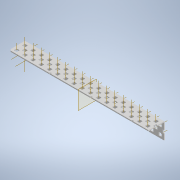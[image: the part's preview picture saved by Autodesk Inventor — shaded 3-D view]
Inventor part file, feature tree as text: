
AUTODESK INVENTOR PART (.ipt)
format: ipt  version: 2020 (Build 240168000, 168)  size: 2,144,256 bytes
history: native  units: in
note: dims shown in document units (in); Inventor stores cm internally (conversion verified against a paired STEP export)
features: other x107, pattern_linear x4, plane x2, sheet_metal_op x1, extrude x1, split x1, imported_body x1, sketch x1
ambient origin geometry x8: Origin, YZ Plane, XZ Plane, XY Plane, X Axis, Y Axis, Z Axis, Center Point
bodies: Body1 (feature_tree)
feature tree (118):
  sheet_metal_op  "Fold1"
  other  "L-Channel"
  extrude  "length cut"  Depth=0.5in
  other  "top out axis"
  other  "top inner axis"
  other  "back out axis"
  other  "back inner axis"
  pattern_linear  "top outer axes"  Count1=2 Spacing1=0.5in
  pattern_linear  "top inner axes"  Spacing1=0.5in  [1 undecoded]
  pattern_linear  "back outer axes"  Count1=2 Spacing1=0.5in
  pattern_linear  "back inner axes"  Spacing1=0.5in  [1 undecoded]
  other  "right plane"
  plane  "Work Plane3"
  split  "Split1"
  plane  "Work Plane5"
  imported_body  "Base1"
  sketch  "Sketch1"  dims[d1=0.0in d4=0.5in d5=0.7874in d7=0.5in d10=0.5in d13=0.5in d14=0.7874in d16=0.5in d19=0.5in d20=-9.0in d21=0.0in d22=0.0in d23=0.0in d24=0.0in d25=0.0in d26=0.0in]
  other  "Work Point1"
  other  "Work Point2"
  other  "Work Point3"
  other  "Work Point4"
  other  "Work Axis5"
  other  "Work Axis6"
  other  "Work Axis7"
  other  "Work Axis8"
  other  "Work Axis11"
  other  "Work Axis12"
  other  "Work Axis13"
  other  "Work Axis14"
  other  "Work Axis15"
  other  "Work Axis18"
  other  "Work Axis19"
  other  "Work Axis20"
  other  "Work Axis23"
  other  "Work Axis24"
  other  "Work Axis25"
  other  "Work Axis26"
  other  "Work Axis29"
  other  "Work Axis30"
  other  "Work Axis31"
  other  "Work Axis32"
  other  "Work Axis33"
  other  "Work Axis36"
  other  "Work Axis37"
  other  "Work Axis38"
  other  "Work Axis41"
  other  "Work Axis42"
  other  "Work Axis43"
  other  "Work Axis44"
  other  "Work Axis45"
  other  "Work Axis46"
  other  "Work Axis47"
  other  "Work Axis48"
  other  "Work Axis49"
  other  "Work Axis50"
  other  "Work Axis51"
  other  "Work Axis52"
  other  "Work Axis61"
  other  "Work Axis62"
  other  "Work Axis63"
  other  "Work Axis64"
  other  "Work Axis65"
  other  "Work Axis66"
  other  "Work Axis67"
  other  "Work Axis68"
  other  "Work Axis69"
  other  "Work Axis70"
  other  "Work Axis71"
  other  "Work Axis72"
  other  "Work Axis81"
  other  "Work Axis82"
  other  "Work Axis83"
  other  "Work Axis84"
  other  "Work Axis85"
  other  "Work Axis86"
  other  "Work Axis87"
  other  "Work Axis88"
  other  "Work Axis89"
  other  "Work Axis90"
  other  "Work Axis91"
  other  "Work Axis92"
  other  "Work Axis101"
  other  "Work Axis102"
  other  "Work Axis103"
  other  "Work Axis104"
  other  "Work Axis105"
  other  "Work Axis106"
  other  "Work Axis107"
  other  "Work Axis108"
  other  "Work Axis109"
  other  "Work Axis110"
  other  "Work Axis111"
  other  "Work Axis112"
  other  "Work Axis121"
  other  "Work Axis122"
  other  "Work Axis123"
  other  "Work Axis124"
  other  "Work Axis125"
  other  "Work Axis126"
  other  "Work Axis127"
  other  "Work Axis128"
  other  "Work Axis129"
  other  "Work Axis130"
  other  "Work Axis131"
  other  "Work Axis132"
  other  "Work Axis141"
  other  "Work Axis142"
  other  "Work Axis143"
  other  "Work Axis144"
  other  "Work Axis145"
  other  "Work Axis146"
  other  "Work Axis147"
  other  "Work Axis148"
  other  "Work Axis149"
  other  "Work Axis150"
  other  "Work Axis151"
  other  "Work Axis152"
  other  "left plane"
note: 2 required parameter values undecoded (feature->parameter linkage not recoverable at this tier; creation-order binding heuristic only, values carry confidence <= 0.55)
